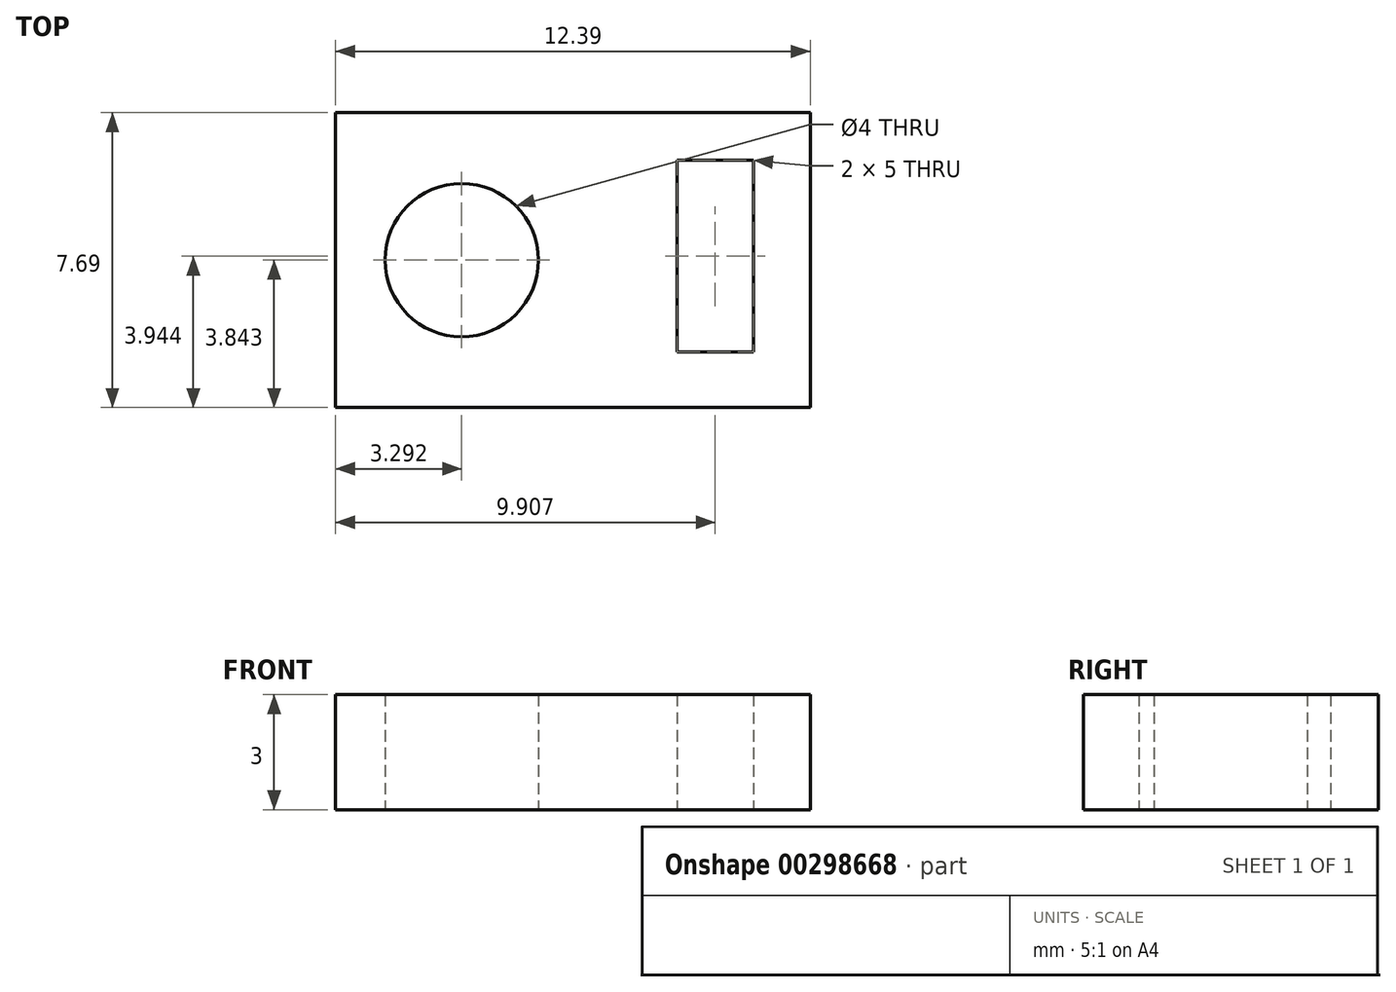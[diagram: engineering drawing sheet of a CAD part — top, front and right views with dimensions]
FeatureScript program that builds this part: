
annotation { "Feature Type Name" : "Feature", "Feature Type Description" : "" }
export const myFeature = defineFeature(function(context is Context, id is Id, definition is map)
    precondition{}
    {
        {
            var Q0;
            Q0=qCreatedBy(makeId("Top.planeOp"),FACE);
            var sketch = newSketch(context, id + "F0", { "sketchPlane" : qUnion([Q0])});
            skLineSegment(sketch, "E0.bottom", {"start": v(-10.14, 9.8) * mm, "end": v(2.25, 9.8) * mm});
            skLineSegment(sketch, "E0.top", {"start": v(-10.14, 2.1) * mm, "end": v(2.25, 2.1) * mm});
            skLineSegment(sketch, "E0.left", {"start": v(-10.14, 9.8) * mm, "end": v(-10.14, 2.1) * mm});
            skLineSegment(sketch, "E0.right", {"start": v(2.25, 9.8) * mm, "end": v(2.25, 2.1) * mm});
            skCircle(sketch, "E1", {"center": v(-6.85, 5.95) * mm, "radius": 2 * mm});
            skPoint(sketch, "E1.centerSnap0", {"position": v(-10.14, 5.95) * mm});
            skLineSegment(sketch, "E2.bottom", {"start": v(-1.23, 8.55) * mm, "end": v(0.77, 8.55) * mm});
            skLineSegment(sketch, "E2.top", {"start": v(-1.23, 3.55) * mm, "end": v(0.77, 3.55) * mm});
            skLineSegment(sketch, "E2.left", {"start": v(-1.23, 8.55) * mm, "end": v(-1.23, 3.55) * mm});
            skLineSegment(sketch, "E2.right", {"start": v(0.77, 8.55) * mm, "end": v(0.77, 3.55) * mm});
            skSolve(sketch);
        }
        {
            var Q0;
            Q0=qSketchRegion(id+"F0",true);
            extrude(context, id + "F1", {"entities" : qUnion([Q0]), "depth" : 3 * mm});
        }
    });
